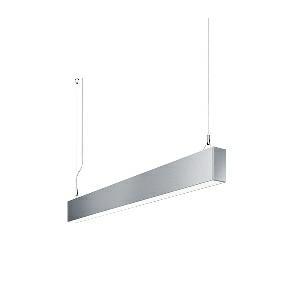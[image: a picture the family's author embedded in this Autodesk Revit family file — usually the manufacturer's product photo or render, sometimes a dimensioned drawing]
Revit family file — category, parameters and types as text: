
# Revit family: dotoo_line_-_dlp_1000_830_d_00805839_57aa
name_source: partatom
category: Lighting Fixtures
units: mm (PartAtom-declared; Revit-internal decimal feet)

## family parameters
Cut with Voids When Loaded = No
Host = Face
Light Source = No
Part Type = Normal
Room Calculation Point = No
Round Connector Dimension = Use Diameter
Shared = No

## types (1)
- DOTOO.line - DLP 1000/830/D (1 x LED, 1000 lm, 3000K)
    Apparent Load = 10 VA
    Approval mark = CE
    CIE Flux Codes = 67 91 98 100 100
    Color Rendering = 80-89
    Color Temperature = 3000K
    Control Gear = Electronic ballast
    Default Elevation = 1800 mm
    Description = DLP 1000/830/D|Suspended luminaire|light source: LED|connected load: 220-240 V, 50/60 Hz|Power consumption: approx. 10 W|standby: approx. 0,20|luminous flux: 1000 lm|luminous efficacy: 100 lm/W|light distribution: Direct|direct ratio: approx. 100 %|colour temperature: Warm white, ca. 3000 K|color rendering index (CRI): >= 80|chromaticity tolerance:  3 SDCM|System of protection: IP 40|technology: Continuously dimmable|luminaire body|material: Sectional aluminium|colour: Silver|lamp cover: Acrylic (PMMA), Clear|mains lead: 2.00 m With free stranded wires|Fastening: Steel cable 0.3 - 0.7 m|glare control: Prism aperture|luminance(L65): <= 3000 cd/m|unified glare rating(4H 8H): <=  19|special features: DALI Load 1x, TouchDIM - dimming via standard switch, Flicker-free, Suitable as emergency lighting|
    Frequency = 50 Hz
    Height = 110 mm
    Lamp = 1 x LED
    Lamp Light Flux = 1000 lm
    Lamp count = 1
    Length = 854 mm
    Luminous efficacy = 100 lm/W
    Manufacturer = Waldmann
    ModVariant = No
    Model = 00805839
    Mounting Place = Ceiling
    Mounting Type = Pendant
    Number of Poles = 1
    OnlyDefault = Yes
    Power Factor = 1
    Product Name = DOTOO.line - DLP 1000/830/D
    Product group = Suspended luminaire
    ProductGroupID = 9
    Protection Class = Protection class I
    Protection Degree = IP 40
    RLX_Detail_Level = 1
    RLX_Emergency_Light_Flux = 0 lm
    RLX_Emergency_Type = 0
    RLX_Emergency_Type_DB = No
    RlxData = <blob elided: 19701 chars, md5=0c2a7e2f>
    Socket = socket
    Standby Power = 0 W
    System Light Flux = 1000 lm
    System Power = 10 W
    Type Comments = Product without accessories
    Type Image = 113288000-00692512.jpg
    URL = http://relux.com
    VarID = ---
    Voltage = 230 V
    Voltage Range = 220-240 V
    Weight = 0.00 kg
    Width = 60 mm  [stored 0.19685 ft]

note: [stored X ft] marks values corroborated as IEEE doubles in the binary element streams (Revit-internal decimal feet)

## geometry (parser evidence)
native form markers: Blend x4, Sweep x11
no freeform markers — native parametric forms only
